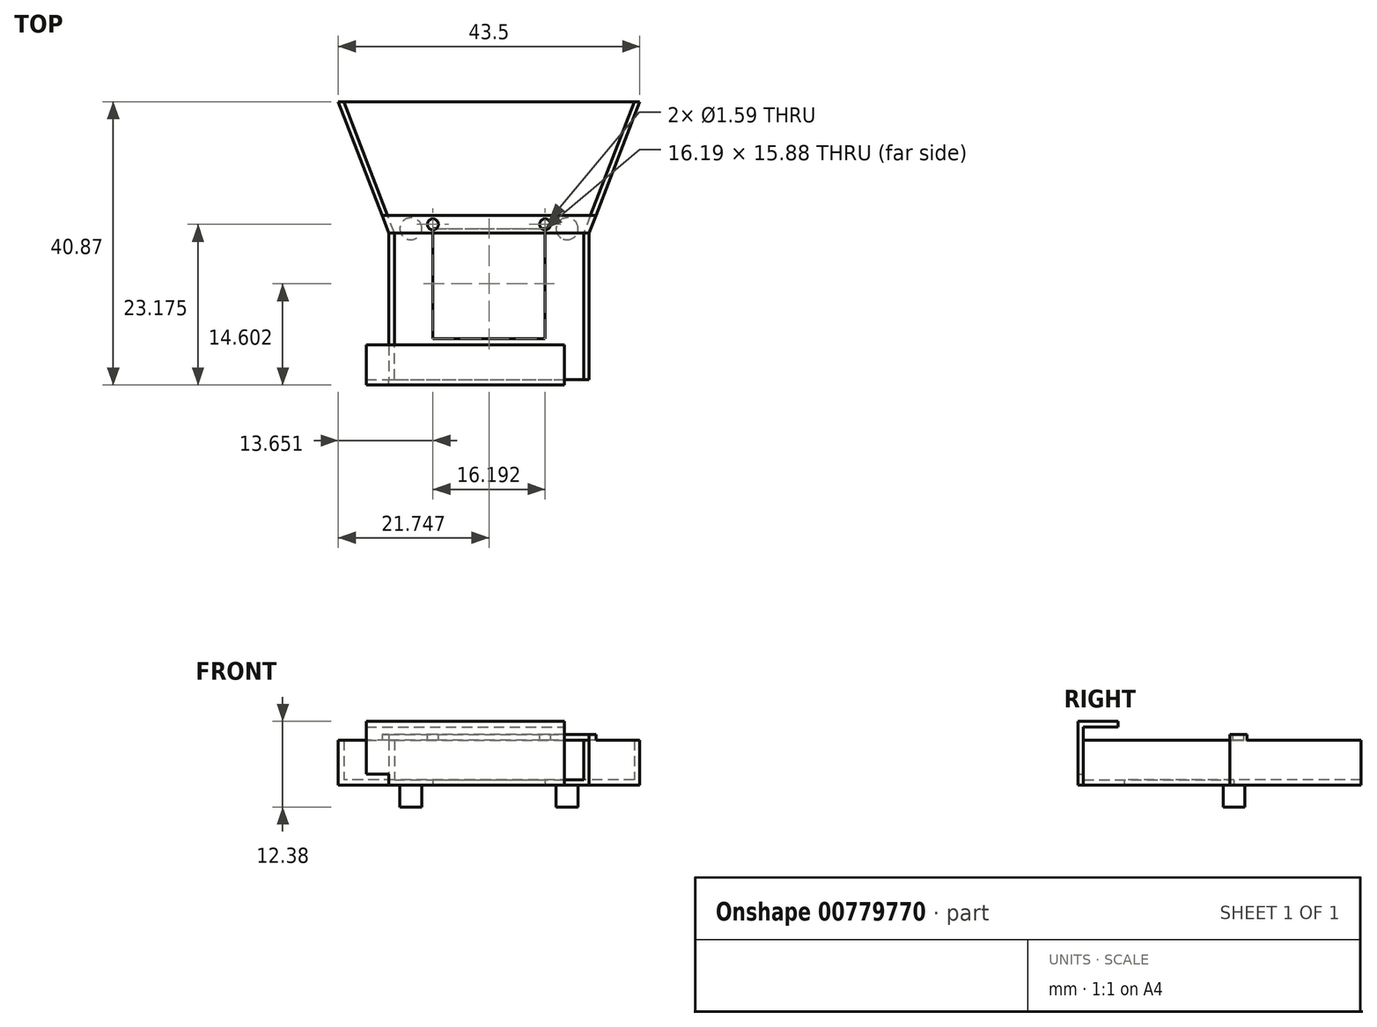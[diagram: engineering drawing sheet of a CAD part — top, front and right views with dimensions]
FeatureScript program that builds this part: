
annotation { "Feature Type Name" : "Feature", "Feature Type Description" : "" }
export const myFeature = defineFeature(function(context is Context, id is Id, definition is map)
    precondition{}
    {
        {
            var Q0;
            Q0=qCreatedBy(makeId("Top.planeOp"),FACE);
            var sketch = newSketch(context, id + "F0", { "sketchPlane" : qUnion([Q0])});
            skLineSegment(sketch, "E0", {"start": v(-18.37, 27.4) * mm, "end": v(-18.37, 7.09) * mm});
            skLineSegment(sketch, "E1", {"start": v(-18.37, 7.09) * mm, "end": v(10.52, 7.09) * mm});
            skLineSegment(sketch, "E2", {"start": v(10.52, 7.09) * mm, "end": v(10.52, 27.4) * mm});
            skLineSegment(sketch, "E3", {"start": v(10.52, 27.4) * mm, "end": v(17.83, 46.37) * mm});
            skLineSegment(sketch, "E4", {"start": v(17.83, 46.37) * mm, "end": v(-25.67, 46.37) * mm});
            skLineSegment(sketch, "E5", {"start": v(-25.67, 46.37) * mm, "end": v(-18.37, 27.4) * mm});
            skLineSegment(sketch, "E6.bottom", {"start": v(-12.02, 28.04) * mm, "end": v(4.17, 28.04) * mm});
            skLineSegment(sketch, "E6.top", {"start": v(-12.02, 12.17) * mm, "end": v(4.17, 12.17) * mm});
            skLineSegment(sketch, "E6.left", {"start": v(-12.02, 28.04) * mm, "end": v(-12.02, 12.17) * mm});
            skLineSegment(sketch, "E6.right", {"start": v(4.17, 28.04) * mm, "end": v(4.17, 12.17) * mm});
            skSolve(sketch);
        }
        {
            var Q0;
            Q0=makeQuery(id+"F0.imprint","IMPRINT",FACE,{"disambiguationData":[TD([[makeQuery(id+"F0.imprint","IMPRINT",EDGE,{"derivedFrom":sQuery(id+"F0.wireOp",EDGE,"E0")}),1.0]])]});
            extrude(context, id + "F1", {"entities" : qUnion([Q0]), "depth" : 0.32 * mm, "offsetDistance" : 25.4 * mm});
        }
        {
            var Q0;
            Q0=makeQuery(id+"F1.opExtrude","CAP_FACE",FACE,{"disambiguationData":[OSD([sQuery(id+"F0.wireOp",EDGE,"E0"),sQuery(id+"F0.wireOp",EDGE,"E1"),sQuery(id+"F0.wireOp",EDGE,"E2"),sQuery(id+"F0.wireOp",EDGE,"E3"),sQuery(id+"F0.wireOp",EDGE,"E4"),sQuery(id+"F0.wireOp",EDGE,"E5"),sQuery(id+"F0.wireOp",EDGE,"E6.bottom"),sQuery(id+"F0.wireOp",EDGE,"E6.top"),sQuery(id+"F0.wireOp",EDGE,"E6.left"),sQuery(id+"F0.wireOp",EDGE,"E6.right")])],"isStart":false});
            var sketch = newSketch(context, id + "F2", { "sketchPlane" : qUnion([Q0])});
            skLineSegment(sketch, "E7", {"start": v(-25.67, 46.37) * mm, "end": v(-18.37, 27.4) * mm});
            skLineSegment(sketch, "E8", {"start": v(-18.37, 27.4) * mm, "end": v(-18.37, 7.09) * mm});
            skLineSegment(sketch, "E9", {"start": v(-18.37, 7.09) * mm, "end": v(-17.58, 7.09) * mm});
            skLineSegment(sketch, "E10", {"start": v(-17.58, 7.09) * mm, "end": v(-17.58, 27.4) * mm});
            skLineSegment(sketch, "E11", {"start": v(-17.58, 27.4) * mm, "end": v(-24.88, 46.37) * mm});
            skLineSegment(sketch, "E12", {"start": v(-24.88, 46.37) * mm, "end": v(-25.67, 46.37) * mm});
            skLineSegment(sketch, "E13", {"start": v(10.52, 7.09) * mm, "end": v(10.52, 27.4) * mm});
            skLineSegment(sketch, "E14", {"start": v(10.52, 27.4) * mm, "end": v(17.83, 46.37) * mm});
            skLineSegment(sketch, "E15", {"start": v(17.83, 46.37) * mm, "end": v(17.03, 46.37) * mm});
            skLineSegment(sketch, "E16", {"start": v(17.03, 46.37) * mm, "end": v(9.73, 27.4) * mm});
            skLineSegment(sketch, "E17", {"start": v(9.73, 27.4) * mm, "end": v(9.73, 7.09) * mm});
            skLineSegment(sketch, "E18", {"start": v(9.73, 7.09) * mm, "end": v(10.52, 7.09) * mm});
            skSolve(sketch);
        }
        {
            var Q0;
            Q0=makeQuery(id+"F2.imprint","IMPRINT",FACE,{"disambiguationData":[TD([[makeQuery(id+"F2.imprint","IMPRINT",EDGE,{"derivedFrom":sQuery(id+"F2.wireOp",EDGE,"E13")}),1.0]])]});
            var Q1;
            Q1=makeQuery(id+"F2.imprint","IMPRINT",FACE,{"disambiguationData":[TD([[makeQuery(id+"F2.imprint","IMPRINT",EDGE,{"derivedFrom":sQuery(id+"F2.wireOp",EDGE,"E7")}),1.0]])]});
            extrude(context, id + "F3", {"entities" : qUnion([Q0, Q1]), "operationType" : NewBodyOperationType.ADD, "depth" : 5.7 * mm, "offsetDistance" : 25.4 * mm});
        }
        {
            var Q0;
            Q0=makeQuery(id+"F3.opExtrude","CAP_FACE",FACE,{"disambiguationData":[OSD([sQuery(id+"F2.wireOp",EDGE,"E7"),sQuery(id+"F2.wireOp",EDGE,"E8"),sQuery(id+"F2.wireOp",EDGE,"E9"),sQuery(id+"F2.wireOp",EDGE,"E10"),sQuery(id+"F2.wireOp",EDGE,"E11"),sQuery(id+"F2.wireOp",EDGE,"E12")])],"isStart":false});
            var sketch = newSketch(context, id + "F4", { "sketchPlane" : qUnion([Q0])});
            skLineSegment(sketch, "E19", {"start": v(-18.37, 27.4) * mm, "end": v(10.52, 27.4) * mm});
            skLineSegment(sketch, "E20", {"start": v(10.52, 27.4) * mm, "end": v(11.5, 29.95) * mm});
            skLineSegment(sketch, "E21", {"start": v(11.5, 29.95) * mm, "end": v(-19.35, 29.95) * mm});
            skLineSegment(sketch, "E22", {"start": v(-19.35, 29.95) * mm, "end": v(-18.37, 27.4) * mm});
            skSolve(sketch);
        }
        {
            var Q0;
            Q0 = qSketchRegion(id + "F4", true);
            extrude(context, id + "F5", {"entities" : qUnion([Q0]), "operationType" : NewBodyOperationType.ADD, "depth" : 0.8 * mm, "offsetDistance" : 25.4 * mm});
        }
        {
            var Q0;
            Q0=makeQuery(id+"F5.opExtrude","CAP_FACE",FACE,{"disambiguationData":[OSD([sQuery(id+"F4.wireOp",EDGE,"E19"),sQuery(id+"F4.wireOp",EDGE,"E20"),sQuery(id+"F4.wireOp",EDGE,"E21"),sQuery(id+"F4.wireOp",EDGE,"E22")])],"isStart":false});
            var sketch = newSketch(context, id + "F6", { "sketchPlane" : qUnion([Q0])});
            skCircle(sketch, "E23", {"center": v(-12.02, 28.68) * mm, "radius": 0.8 * mm});
            skCircle(sketch, "E24", {"center": v(4.17, 28.68) * mm, "radius": 0.8 * mm});
            skSolve(sketch);
        }
        {
            var Q0;
            Q0=makeQuery(id+"F6.imprint","IMPRINT",FACE,{"disambiguationData":[TD([[makeQuery(id+"F6.imprint","IMPRINT",EDGE,{"derivedFrom":sQuery(id+"F6.wireOp",EDGE,"E23")}),1.0]])]});
            var Q1;
            Q1=makeQuery(id+"F6.imprint","IMPRINT",FACE,{"disambiguationData":[TD([[makeQuery(id+"F6.imprint","IMPRINT",EDGE,{"derivedFrom":sQuery(id+"F6.wireOp",EDGE,"E24")}),1.0]])]});
            extrude(context, id + "F7", {"entities" : qUnion([Q0, Q1]), "operationType" : NewBodyOperationType.REMOVE, "oppositeDirection" : true, "depth" : 0.8 * mm, "offsetDistance" : 25.4 * mm});
        }
        {
            var Q0;
            Q0=makeQuery(id+"F1.opExtrude","CAP_FACE",FACE,{"disambiguationData":[OSD([sQuery(id+"F0.wireOp",EDGE,"E0"),sQuery(id+"F0.wireOp",EDGE,"E1"),sQuery(id+"F0.wireOp",EDGE,"E2"),sQuery(id+"F0.wireOp",EDGE,"E3"),sQuery(id+"F0.wireOp",EDGE,"E4"),sQuery(id+"F0.wireOp",EDGE,"E5"),sQuery(id+"F0.wireOp",EDGE,"E6.bottom"),sQuery(id+"F0.wireOp",EDGE,"E6.top"),sQuery(id+"F0.wireOp",EDGE,"E6.left"),sQuery(id+"F0.wireOp",EDGE,"E6.right")])],"isStart":true});
            extrude(context, id + "F8", {"entities" : qUnion([Q0]), "operationType" : NewBodyOperationType.ADD, "depth" : 0.32 * mm, "offsetDistance" : 25.4 * mm});
        }
        {
            var Q0;
            {var subQ0=sQuery(id+"F0.wireOp",EDGE,"E1");Q0=makeQuery(id+"F8.boolean.opBoolean","MERGE",FACE,{"derivedFrom":[makeQuery(id+"F3.boolean.opBoolean","MERGE",FACE,{"derivedFrom":[makeQuery(id+"F1.opExtrude","SWEPT_FACE",FACE,{"disambiguationData":[OSD([subQ0])]}),makeQuery(id+"F3.opExtrude","SWEPT_FACE",FACE,{"disambiguationData":[OSD([sQuery(id+"F2.wireOp",EDGE,"E9")])]}),makeQuery(id+"F3.opExtrude","SWEPT_FACE",FACE,{"disambiguationData":[OSD([sQuery(id+"F2.wireOp",EDGE,"E18")])]})]}),makeQuery(id+"F8.opExtrude","SWEPT_FACE",FACE,{"disambiguationData":[OSD([subQ0])]})]});}
            var sketch = newSketch(context, id + "F9", { "sketchPlane" : qUnion([Q0])});
            skLineSegment(sketch, "E25.bottom", {"start": v(-18.37, 0.32) * mm, "end": v(-16.78, 0.32) * mm});
            skLineSegment(sketch, "E25.top", {"start": v(-18.37, -0.32) * mm, "end": v(-16.78, -0.32) * mm});
            skLineSegment(sketch, "E25.left", {"start": v(-18.37, 0.32) * mm, "end": v(-18.37, -0.32) * mm});
            skLineSegment(sketch, "E25.right", {"start": v(-16.78, 0.32) * mm, "end": v(-16.78, -0.32) * mm});
            skLineSegment(sketch, "E26.bottom", {"start": v(-15.2, 0.32) * mm, "end": v(-13.6, 0.32) * mm});
            skLineSegment(sketch, "E26.top", {"start": v(-15.2, -0.32) * mm, "end": v(-13.6, -0.32) * mm});
            skLineSegment(sketch, "E26.left", {"start": v(-15.2, 0.32) * mm, "end": v(-15.2, -0.32) * mm});
            skLineSegment(sketch, "E26.right", {"start": v(-13.6, 0.32) * mm, "end": v(-13.6, -0.32) * mm});
            skLineSegment(sketch, "E27.bottom", {"start": v(5.35, 0.32) * mm, "end": v(3.76, 0.32) * mm});
            skLineSegment(sketch, "E27.top", {"start": v(5.35, -0.32) * mm, "end": v(3.76, -0.32) * mm});
            skLineSegment(sketch, "E27.left", {"start": v(5.35, 0.32) * mm, "end": v(5.35, -0.32) * mm});
            skLineSegment(sketch, "E27.right", {"start": v(3.76, 0.32) * mm, "end": v(3.76, -0.32) * mm});
            skLineSegment(sketch, "E28.bottom", {"start": v(2.17, 0.32) * mm, "end": v(0.59, 0.32) * mm});
            skLineSegment(sketch, "E28.top", {"start": v(2.17, -0.32) * mm, "end": v(0.59, -0.32) * mm});
            skLineSegment(sketch, "E28.left", {"start": v(2.17, 0.32) * mm, "end": v(2.17, -0.32) * mm});
            skLineSegment(sketch, "E28.right", {"start": v(0.59, 0.32) * mm, "end": v(0.59, -0.32) * mm});
            skSolve(sketch);
        }
        {
            var Q0;
            Q0=makeQuery(id+"F9.imprint","IMPRINT",FACE,{"disambiguationData":[TD([[makeQuery(id+"F9.imprint","IMPRINT",EDGE,{"derivedFrom":sQuery(id+"F9.wireOp",EDGE,"E25.bottom")}),-1.0]])]});
            var Q1;
            Q1=makeQuery(id+"F9.imprint","IMPRINT",FACE,{"disambiguationData":[TD([[makeQuery(id+"F9.imprint","IMPRINT",EDGE,{"derivedFrom":sQuery(id+"F9.wireOp",EDGE,"E26.bottom")}),-1.0]])]});
            var Q2;
            Q2=makeQuery(id+"F9.imprint","IMPRINT",FACE,{"disambiguationData":[TD([[makeQuery(id+"F9.imprint","IMPRINT",EDGE,{"derivedFrom":sQuery(id+"F9.wireOp",EDGE,"E28.bottom")}),-1.0]])]});
            var Q3;
            Q3=makeQuery(id+"F9.imprint","IMPRINT",FACE,{"disambiguationData":[TD([[makeQuery(id+"F9.imprint","IMPRINT",EDGE,{"derivedFrom":sQuery(id+"F9.wireOp",EDGE,"E27.bottom")}),-1.0]])]});
            extrude(context, id + "F10", {"entities" : qUnion([Q0, Q1, Q2, Q3]), "operationType" : NewBodyOperationType.ADD, "depth" : 1.59 * mm, "offsetDistance" : 25.4 * mm});
        }
        {
            var Q0;
            Q0=makeQuery(id+"F10.boolean.opBoolean","MERGE",FACE,{"derivedFrom":[makeQuery(id+"F8.opExtrude","CAP_FACE",FACE,{"disambiguationData":[OSD([sQuery(id+"F0.wireOp",EDGE,"E0"),sQuery(id+"F0.wireOp",EDGE,"E1"),sQuery(id+"F0.wireOp",EDGE,"E2"),sQuery(id+"F0.wireOp",EDGE,"E3"),sQuery(id+"F0.wireOp",EDGE,"E4"),sQuery(id+"F0.wireOp",EDGE,"E5"),sQuery(id+"F0.wireOp",EDGE,"E6.bottom"),sQuery(id+"F0.wireOp",EDGE,"E6.top"),sQuery(id+"F0.wireOp",EDGE,"E6.left"),sQuery(id+"F0.wireOp",EDGE,"E6.right")])],"isStart":false}),makeQuery(id+"F10.opExtrude","SWEPT_FACE",FACE,{"disambiguationData":[OSD([sQuery(id+"F9.wireOp",EDGE,"E25.top")])]}),makeQuery(id+"F10.opExtrude","SWEPT_FACE",FACE,{"disambiguationData":[OSD([sQuery(id+"F9.wireOp",EDGE,"E26.top")])]}),makeQuery(id+"F10.opExtrude","SWEPT_FACE",FACE,{"disambiguationData":[OSD([sQuery(id+"F9.wireOp",EDGE,"E27.top")])]}),makeQuery(id+"F10.opExtrude","SWEPT_FACE",FACE,{"disambiguationData":[OSD([sQuery(id+"F9.wireOp",EDGE,"E28.top")])]})]});
            extrude(context, id + "F11", {"entities" : qUnion([Q0]), "operationType" : NewBodyOperationType.ADD, "depth" : 0.32 * mm, "offsetDistance" : 25.4 * mm});
        }
        {
            var Q0;
            Q0=makeQuery(id+"F10.boolean.opBoolean","MERGE",FACE,{"derivedFrom":[makeQuery(id+"F1.opExtrude","CAP_FACE",FACE,{"disambiguationData":[OSD([sQuery(id+"F0.wireOp",EDGE,"E0"),sQuery(id+"F0.wireOp",EDGE,"E1"),sQuery(id+"F0.wireOp",EDGE,"E2"),sQuery(id+"F0.wireOp",EDGE,"E3"),sQuery(id+"F0.wireOp",EDGE,"E4"),sQuery(id+"F0.wireOp",EDGE,"E5"),sQuery(id+"F0.wireOp",EDGE,"E6.bottom"),sQuery(id+"F0.wireOp",EDGE,"E6.top"),sQuery(id+"F0.wireOp",EDGE,"E6.left"),sQuery(id+"F0.wireOp",EDGE,"E6.right")])],"isStart":false}),makeQuery(id+"F10.opExtrude","SWEPT_FACE",FACE,{"disambiguationData":[OSD([sQuery(id+"F9.wireOp",EDGE,"E25.bottom")])]}),makeQuery(id+"F10.opExtrude","SWEPT_FACE",FACE,{"disambiguationData":[OSD([sQuery(id+"F9.wireOp",EDGE,"E26.bottom")])]}),makeQuery(id+"F10.opExtrude","SWEPT_FACE",FACE,{"disambiguationData":[OSD([sQuery(id+"F9.wireOp",EDGE,"E27.bottom")])]}),makeQuery(id+"F10.opExtrude","SWEPT_FACE",FACE,{"disambiguationData":[OSD([sQuery(id+"F9.wireOp",EDGE,"E28.bottom")])]})]});
            var sketch = newSketch(context, id + "F12", { "sketchPlane" : qUnion([Q0])});
            skLineSegment(sketch, "E29.bottom", {"start": v(-16.78, 7.09) * mm, "end": v(-18.37, 7.09) * mm});
            skLineSegment(sketch, "E29.top", {"start": v(-16.78, 5.5) * mm, "end": v(-18.37, 5.5) * mm});
            skLineSegment(sketch, "E29.left", {"start": v(-16.78, 7.09) * mm, "end": v(-16.78, 5.5) * mm});
            skLineSegment(sketch, "E29.right", {"start": v(-18.37, 7.09) * mm, "end": v(-18.37, 5.5) * mm});
            skLineSegment(sketch, "E30.bottom", {"start": v(-15.2, 7.09) * mm, "end": v(-13.6, 7.09) * mm});
            skLineSegment(sketch, "E30.top", {"start": v(-15.2, 5.5) * mm, "end": v(-13.6, 5.5) * mm});
            skLineSegment(sketch, "E30.left", {"start": v(-15.2, 7.09) * mm, "end": v(-15.2, 5.5) * mm});
            skLineSegment(sketch, "E30.right", {"start": v(-13.6, 7.09) * mm, "end": v(-13.6, 5.5) * mm});
            skLineSegment(sketch, "E31.bottom", {"start": v(0.59, 7.09) * mm, "end": v(2.17, 7.09) * mm});
            skLineSegment(sketch, "E31.top", {"start": v(0.59, 5.5) * mm, "end": v(2.17, 5.5) * mm});
            skLineSegment(sketch, "E31.left", {"start": v(0.59, 7.09) * mm, "end": v(0.59, 5.5) * mm});
            skLineSegment(sketch, "E31.right", {"start": v(2.17, 7.09) * mm, "end": v(2.17, 5.5) * mm});
            skLineSegment(sketch, "E32.bottom", {"start": v(3.76, 7.09) * mm, "end": v(5.35, 7.09) * mm});
            skLineSegment(sketch, "E32.top", {"start": v(3.76, 5.5) * mm, "end": v(5.35, 5.5) * mm});
            skLineSegment(sketch, "E32.left", {"start": v(3.76, 7.09) * mm, "end": v(3.76, 5.5) * mm});
            skLineSegment(sketch, "E32.right", {"start": v(5.35, 7.09) * mm, "end": v(5.35, 5.5) * mm});
            skSolve(sketch);
        }
        {
            var Q0;
            Q0 = qSketchRegion(id + "F12", true);
            extrude(context, id + "F13", {"entities" : qUnion([Q0]), "operationType" : NewBodyOperationType.ADD, "depth" : 0.8 * mm, "offsetDistance" : 25.4 * mm});
        }
        {
            var Q0;
            Q0=makeQuery(id+"F11.opExtrude","CAP_FACE",FACE,{"disambiguationData":[OSD([sQuery(id+"F0.wireOp",EDGE,"E0"),sQuery(id+"F0.wireOp",EDGE,"E1"),sQuery(id+"F0.wireOp",EDGE,"E2"),sQuery(id+"F0.wireOp",EDGE,"E3"),sQuery(id+"F0.wireOp",EDGE,"E4"),sQuery(id+"F0.wireOp",EDGE,"E5"),sQuery(id+"F0.wireOp",EDGE,"E6.bottom"),sQuery(id+"F0.wireOp",EDGE,"E6.top"),sQuery(id+"F0.wireOp",EDGE,"E6.left"),sQuery(id+"F0.wireOp",EDGE,"E6.right"),sQuery(id+"F9.wireOp",EDGE,"E25.top"),sQuery(id+"F9.wireOp",EDGE,"E26.top"),sQuery(id+"F9.wireOp",EDGE,"E27.top"),sQuery(id+"F9.wireOp",EDGE,"E28.top")])],"isStart":false});
            extrude(context, id + "F14", {"entities" : qUnion([Q0]), "operationType" : NewBodyOperationType.REMOVE, "oppositeDirection" : true, "depth" : 0.16 * mm, "offsetDistance" : 25.4 * mm});
        }
        {
            var Q0;
            {var subQ0=sQuery(id+"F9.wireOp",EDGE,"E25.left");var subQ1=sQuery(id+"F0.wireOp",EDGE,"E0");Q0=makeQuery(id+"F13.boolean.opBoolean","MERGE",FACE,{"derivedFrom":[makeQuery(id+"F11.boolean.opBoolean","MERGE",FACE,{"derivedFrom":[makeQuery(id+"F10.boolean.opBoolean","MERGE",FACE,{"derivedFrom":[makeQuery(id+"F8.boolean.opBoolean","MERGE",FACE,{"derivedFrom":[makeQuery(id+"F3.boolean.opBoolean","MERGE",FACE,{"derivedFrom":[makeQuery(id+"F1.opExtrude","SWEPT_FACE",FACE,{"disambiguationData":[OSD([subQ1])]}),makeQuery(id+"F3.opExtrude","SWEPT_FACE",FACE,{"disambiguationData":[OSD([sQuery(id+"F2.wireOp",EDGE,"E8")])]})]}),makeQuery(id+"F8.opExtrude","SWEPT_FACE",FACE,{"disambiguationData":[OSD([subQ1])]})]}),makeQuery(id+"F10.opExtrude","SWEPT_FACE",FACE,{"disambiguationData":[OSD([subQ0])]})]}),makeQuery(id+"F11.opExtrude","SWEPT_FACE",FACE,{"disambiguationData":[OSD([subQ1,sQuery(id+"F9.wireOp",EDGE,"E25.top"),subQ0])]})]}),makeQuery(id+"F13.opExtrude","SWEPT_FACE",FACE,{"disambiguationData":[OSD([sQuery(id+"F12.wireOp",EDGE,"E29.right")])]})]});}
            var sketch = newSketch(context, id + "F15", { "sketchPlane" : qUnion([Q0])});
            skCircle(sketch, "E33", {"center": v(-6.3, 0.32) * mm, "radius": 0.5 * mm});
            skPoint(sketch, "E33.centerSnap0", {"position": v(-5.5, 0.32) * mm});
            skPoint(sketch, "E33.centerSnap1", {"position": v(-6.3, 1.11) * mm});
            skSolve(sketch);
        }
        {
            var Q0;
            Q0=makeQuery(id+"F15.imprint","IMPRINT",FACE,{"disambiguationData":[TD([[makeQuery(id+"F15.imprint","IMPRINT",EDGE,{"derivedFrom":sQuery(id+"F15.wireOp",EDGE,"E33")}),1.0]])]});
            extrude(context, id + "F16", {"entities" : qUnion([Q0]), "operationType" : NewBodyOperationType.REMOVE, "oppositeDirection" : true, "depth" : 25.4 * mm, "offsetDistance" : 25.4 * mm});
        }
        {
            var Q0;
            Q0=makeQuery(id+"F14.boolean.opBoolean","COPY",FACE,{"derivedFrom":makeQuery(id+"F14.opExtrude","CAP_FACE",FACE,{"disambiguationData":[OSD([sQuery(id+"F0.wireOp",EDGE,"E0"),sQuery(id+"F0.wireOp",EDGE,"E1"),sQuery(id+"F0.wireOp",EDGE,"E2"),sQuery(id+"F0.wireOp",EDGE,"E3"),sQuery(id+"F0.wireOp",EDGE,"E4"),sQuery(id+"F0.wireOp",EDGE,"E5"),sQuery(id+"F0.wireOp",EDGE,"E6.bottom"),sQuery(id+"F0.wireOp",EDGE,"E6.top"),sQuery(id+"F0.wireOp",EDGE,"E6.left"),sQuery(id+"F0.wireOp",EDGE,"E6.right"),sQuery(id+"F9.wireOp",EDGE,"E25.top"),sQuery(id+"F9.wireOp",EDGE,"E26.top"),sQuery(id+"F9.wireOp",EDGE,"E27.top"),sQuery(id+"F9.wireOp",EDGE,"E28.top")])],"isStart":false})});
            var sketch = newSketch(context, id + "F17", { "sketchPlane" : qUnion([Q0])});
            skCircle(sketch, "E34", {"center": v(-15.2, -28.04) * mm, "radius": 1.59 * mm});
            skCircle(sketch, "E35", {"center": v(7.35, -28.04) * mm, "radius": 1.59 * mm});
            skSolve(sketch);
        }
        {
            var Q0;
            Q0=makeQuery(id+"F17.imprint","IMPRINT",FACE,{"disambiguationData":[TD([[makeQuery(id+"F17.imprint","IMPRINT",EDGE,{"derivedFrom":sQuery(id+"F17.wireOp",EDGE,"E34")}),1.0]])]});
            var Q1;
            Q1=makeQuery(id+"F17.imprint","IMPRINT",FACE,{"disambiguationData":[TD([[makeQuery(id+"F17.imprint","IMPRINT",EDGE,{"derivedFrom":sQuery(id+"F17.wireOp",EDGE,"E35")}),1.0]])]});
            extrude(context, id + "F18", {"entities" : qUnion([Q0, Q1]), "operationType" : NewBodyOperationType.ADD, "depth" : 3.17 * mm, "offsetDistance" : 25.4 * mm});
        }
        {
            var Q0;
            {var subQ0=sQuery(id+"F9.wireOp",EDGE,"E27.left");Q0=makeQuery(id+"F13.boolean.opBoolean","MERGE",FACE,{"derivedFrom":[makeQuery(id+"F11.boolean.opBoolean","MERGE",FACE,{"derivedFrom":[makeQuery(id+"F10.opExtrude","SWEPT_FACE",FACE,{"disambiguationData":[OSD([subQ0])]}),makeQuery(id+"F11.opExtrude","SWEPT_FACE",FACE,{"disambiguationData":[OSD([sQuery(id+"F0.wireOp",EDGE,"E1"),sQuery(id+"F9.wireOp",EDGE,"E27.top"),subQ0])]})]}),makeQuery(id+"F13.opExtrude","SWEPT_FACE",FACE,{"disambiguationData":[OSD([sQuery(id+"F12.wireOp",EDGE,"E32.right")])]})]});}
            var Q1;
            {var subQ0=sQuery(id+"F9.wireOp",EDGE,"E28.left");Q1=makeQuery(id+"F13.boolean.opBoolean","MERGE",FACE,{"derivedFrom":[makeQuery(id+"F11.boolean.opBoolean","MERGE",FACE,{"derivedFrom":[makeQuery(id+"F10.opExtrude","SWEPT_FACE",FACE,{"disambiguationData":[OSD([subQ0])]}),makeQuery(id+"F11.opExtrude","SWEPT_FACE",FACE,{"disambiguationData":[OSD([sQuery(id+"F0.wireOp",EDGE,"E1"),sQuery(id+"F9.wireOp",EDGE,"E28.top"),subQ0])]})]}),makeQuery(id+"F13.opExtrude","SWEPT_FACE",FACE,{"disambiguationData":[OSD([sQuery(id+"F12.wireOp",EDGE,"E31.right")])]})]});}
            var Q2;
            {var subQ0=sQuery(id+"F9.wireOp",EDGE,"E25.right");Q2=makeQuery(id+"F13.boolean.opBoolean","MERGE",FACE,{"derivedFrom":[makeQuery(id+"F11.boolean.opBoolean","MERGE",FACE,{"derivedFrom":[makeQuery(id+"F10.opExtrude","SWEPT_FACE",FACE,{"disambiguationData":[OSD([subQ0])]}),makeQuery(id+"F11.opExtrude","SWEPT_FACE",FACE,{"disambiguationData":[OSD([sQuery(id+"F0.wireOp",EDGE,"E1"),sQuery(id+"F9.wireOp",EDGE,"E25.top"),subQ0])]})]}),makeQuery(id+"F13.opExtrude","SWEPT_FACE",FACE,{"disambiguationData":[OSD([sQuery(id+"F12.wireOp",EDGE,"E29.left")])]})]});}
            var Q3;
            {var subQ0=sQuery(id+"F9.wireOp",EDGE,"E26.right");Q3=makeQuery(id+"F13.boolean.opBoolean","MERGE",FACE,{"derivedFrom":[makeQuery(id+"F11.boolean.opBoolean","MERGE",FACE,{"derivedFrom":[makeQuery(id+"F10.opExtrude","SWEPT_FACE",FACE,{"disambiguationData":[OSD([subQ0])]}),makeQuery(id+"F11.opExtrude","SWEPT_FACE",FACE,{"disambiguationData":[OSD([sQuery(id+"F0.wireOp",EDGE,"E1"),sQuery(id+"F9.wireOp",EDGE,"E26.top"),subQ0])]})]}),makeQuery(id+"F13.opExtrude","SWEPT_FACE",FACE,{"disambiguationData":[OSD([sQuery(id+"F12.wireOp",EDGE,"E30.right")])]})]});}
            extrude(context, id + "F19", {"entities" : qUnion([Q0, Q1, Q2, Q3]), "operationType" : NewBodyOperationType.ADD, "depth" : 1.59 * mm, "offsetDistance" : 25.4 * mm});
        }
        {
            var Q0;
            Q0=makeQuery(id+"F19.opExtrude","CAP_FACE",FACE,{"disambiguationData":[OSD([sQuery(id+"F0.wireOp",EDGE,"E1"),sQuery(id+"F9.wireOp",EDGE,"E26.top"),sQuery(id+"F9.wireOp",EDGE,"E26.right"),sQuery(id+"F12.wireOp",EDGE,"E30.right")])],"isStart":false});
            extrude(context, id + "F20", {"entities" : qUnion([Q0]), "operationType" : NewBodyOperationType.ADD, "depth" : 12.7 * mm, "offsetDistance" : 25.4 * mm});
        }
        {
            var Q0;
            Q0=makeQuery(id+"F19.opExtrude","CAP_FACE",FACE,{"disambiguationData":[OSD([sQuery(id+"F0.wireOp",EDGE,"E1"),sQuery(id+"F9.wireOp",EDGE,"E27.top"),sQuery(id+"F9.wireOp",EDGE,"E27.left"),sQuery(id+"F12.wireOp",EDGE,"E32.right")])],"isStart":false});
            var sketch = newSketch(context, id + "F21", { "sketchPlane" : qUnion([Q0])});
            skCircle(sketch, "E36", {"center": v(6.3, 0.32) * mm, "radius": 0.5 * mm});
            skSolve(sketch);
        }
        {
            var Q0;
            Q0=makeQuery(id+"F21.imprint","IMPRINT",FACE,{"disambiguationData":[TD([[makeQuery(id+"F21.imprint","IMPRINT",EDGE,{"derivedFrom":sQuery(id+"F21.wireOp",EDGE,"E36")}),1.0]])]});
            extrude(context, id + "F22", {"entities" : qUnion([Q0]), "operationType" : NewBodyOperationType.ADD, "oppositeDirection" : true, "depth" : 25.3 * mm, "offsetDistance" : 25.4 * mm});
        }
        {
            var Q0;
            {var subQ0=sQuery(id+"F9.wireOp",EDGE,"E25.left");var subQ1=sQuery(id+"F0.wireOp",EDGE,"E0");Q0=makeQuery(id+"F22.boolean.opBoolean","MERGE",FACE,{"derivedFrom":[makeQuery(id+"F13.boolean.opBoolean","MERGE",FACE,{"derivedFrom":[makeQuery(id+"F11.boolean.opBoolean","MERGE",FACE,{"derivedFrom":[makeQuery(id+"F10.boolean.opBoolean","MERGE",FACE,{"derivedFrom":[makeQuery(id+"F8.boolean.opBoolean","MERGE",FACE,{"derivedFrom":[makeQuery(id+"F3.boolean.opBoolean","MERGE",FACE,{"derivedFrom":[makeQuery(id+"F1.opExtrude","SWEPT_FACE",FACE,{"disambiguationData":[OSD([subQ1])]}),makeQuery(id+"F3.opExtrude","SWEPT_FACE",FACE,{"disambiguationData":[OSD([sQuery(id+"F2.wireOp",EDGE,"E8")])]})]}),makeQuery(id+"F8.opExtrude","SWEPT_FACE",FACE,{"disambiguationData":[OSD([subQ1])]})]}),makeQuery(id+"F10.opExtrude","SWEPT_FACE",FACE,{"disambiguationData":[OSD([subQ0])]})]}),makeQuery(id+"F11.opExtrude","SWEPT_FACE",FACE,{"disambiguationData":[OSD([subQ1,sQuery(id+"F9.wireOp",EDGE,"E25.top"),subQ0])]})]}),makeQuery(id+"F13.opExtrude","SWEPT_FACE",FACE,{"disambiguationData":[OSD([sQuery(id+"F12.wireOp",EDGE,"E29.right")])]})]}),makeQuery(id+"F22.opExtrude","CAP_FACE",FACE,{"disambiguationData":[OSD([sQuery(id+"F21.wireOp",EDGE,"E36")])],"isStart":false})]});}
            var sketch = newSketch(context, id + "F23", { "sketchPlane" : qUnion([Q0])});
            skLineSegment(sketch, "E37.bottom", {"start": v(-7.09, 1.11) * mm, "end": v(-5.5, 1.11) * mm});
            skLineSegment(sketch, "E37.top", {"start": v(-7.09, -0.48) * mm, "end": v(-5.5, -0.48) * mm});
            skLineSegment(sketch, "E37.left", {"start": v(-7.09, 1.11) * mm, "end": v(-7.09, -0.48) * mm});
            skLineSegment(sketch, "E37.right", {"start": v(-5.5, 1.11) * mm, "end": v(-5.5, -0.48) * mm});
            skSolve(sketch);
        }
        {
            var Q0;
            Q0=makeQuery(id+"F23.imprint","IMPRINT",FACE,{"disambiguationData":[TD([[makeQuery(id+"F23.imprint","IMPRINT",EDGE,{"derivedFrom":sQuery(id+"F23.wireOp",EDGE,"E37.bottom")}),1.0]])]});
            extrude(context, id + "F24", {"entities" : qUnion([Q0]), "operationType" : NewBodyOperationType.ADD, "depth" : 3.27 * mm, "offsetDistance" : 25.4 * mm});
        }
        {
            var Q0;
            {var subQ0=sQuery(id+"F12.wireOp",EDGE,"E30.right");var subQ1=sQuery(id+"F12.wireOp",EDGE,"E32.right");var subQ2=sQuery(id+"F12.wireOp",EDGE,"E31.right");var subQ3=sQuery(id+"F12.wireOp",EDGE,"E29.left");Q0=makeQuery(id+"F24.boolean.opBoolean","MERGE",FACE,{"derivedFrom":[makeQuery(id+"F20.boolean.opBoolean","MERGE",FACE,{"derivedFrom":[makeQuery(id+"F19.boolean.opBoolean","MERGE",FACE,{"derivedFrom":[makeQuery(id+"F13.opExtrude","CAP_FACE",FACE,{"disambiguationData":[OSD([sQuery(id+"F12.wireOp",EDGE,"E29.bottom"),sQuery(id+"F12.wireOp",EDGE,"E29.top"),subQ3,sQuery(id+"F12.wireOp",EDGE,"E29.right")])],"isStart":false}),makeQuery(id+"F13.opExtrude","CAP_FACE",FACE,{"disambiguationData":[OSD([sQuery(id+"F12.wireOp",EDGE,"E30.bottom"),sQuery(id+"F12.wireOp",EDGE,"E30.top"),sQuery(id+"F12.wireOp",EDGE,"E30.left"),subQ0])],"isStart":false}),makeQuery(id+"F19.opExtrude","SWEPT_FACE",FACE,{"disambiguationData":[OSD([subQ3])]}),makeQuery(id+"F19.opExtrude","SWEPT_FACE",FACE,{"disambiguationData":[OSD([subQ0])]})]}),makeQuery(id+"F19.boolean.opBoolean","MERGE",FACE,{"derivedFrom":[makeQuery(id+"F13.opExtrude","CAP_FACE",FACE,{"disambiguationData":[OSD([sQuery(id+"F12.wireOp",EDGE,"E31.bottom"),sQuery(id+"F12.wireOp",EDGE,"E31.top"),sQuery(id+"F12.wireOp",EDGE,"E31.left"),subQ2])],"isStart":false}),makeQuery(id+"F13.opExtrude","CAP_FACE",FACE,{"disambiguationData":[OSD([sQuery(id+"F12.wireOp",EDGE,"E32.bottom"),sQuery(id+"F12.wireOp",EDGE,"E32.top"),sQuery(id+"F12.wireOp",EDGE,"E32.left"),subQ1])],"isStart":false}),makeQuery(id+"F19.opExtrude","SWEPT_FACE",FACE,{"disambiguationData":[OSD([subQ2])]}),makeQuery(id+"F19.opExtrude","SWEPT_FACE",FACE,{"disambiguationData":[OSD([subQ1])]})]}),makeQuery(id+"F20.opExtrude","SWEPT_FACE",FACE,{"disambiguationData":[OSD([subQ0])]})]}),makeQuery(id+"F24.opExtrude","SWEPT_FACE",FACE,{"disambiguationData":[OSD([sQuery(id+"F23.wireOp",EDGE,"E37.bottom")])]})]});}
            var sketch = newSketch(context, id + "F25", { "sketchPlane" : qUnion([Q0])});
            skLineSegment(sketch, "E38.bottom", {"start": v(-21.64, 6.3) * mm, "end": v(6.94, 6.3) * mm});
            skLineSegment(sketch, "E38.top", {"start": v(-21.64, 5.5) * mm, "end": v(6.94, 5.5) * mm});
            skLineSegment(sketch, "E38.left", {"start": v(-21.64, 6.3) * mm, "end": v(-21.64, 5.5) * mm});
            skLineSegment(sketch, "E38.right", {"start": v(6.94, 6.3) * mm, "end": v(6.94, 5.5) * mm});
            skSolve(sketch);
        }
        {
            var Q0;
            Q0=makeQuery(id+"F25.imprint","IMPRINT",FACE,{"disambiguationData":[TD([[makeQuery(id+"F25.imprint","IMPRINT",EDGE,{"derivedFrom":sQuery(id+"F25.wireOp",EDGE,"E38.bottom")}),-1.0]])]});
            extrude(context, id + "F26", {"entities" : qUnion([Q0]), "operationType" : NewBodyOperationType.ADD, "depth" : 7.62 * mm, "offsetDistance" : 25.4 * mm});
        }
        {
            var Q0;
            {var subQ0=sQuery(id+"F12.wireOp",EDGE,"E30.right");var subQ1=sQuery(id+"F12.wireOp",EDGE,"E30.bottom");var subQ2=sQuery(id+"F9.wireOp",EDGE,"E26.right");var subQ3=sQuery(id+"F9.wireOp",EDGE,"E26.top");var subQ4=sQuery(id+"F0.wireOp",EDGE,"E1");var subQ5=sQuery(id+"F12.wireOp",EDGE,"E31.bottom");var subQ6=sQuery(id+"F12.wireOp",EDGE,"E32.bottom");var subQ7=sQuery(id+"F12.wireOp",EDGE,"E29.bottom");Q0=makeQuery(id+"F20.boolean.opBoolean","MERGE",FACE,{"derivedFrom":[makeQuery(id+"F19.boolean.opBoolean","MERGE",FACE,{"derivedFrom":[makeQuery(id+"F13.opExtrude","SWEPT_FACE",FACE,{"disambiguationData":[OSD([subQ1])]}),makeQuery(id+"F13.opExtrude","SWEPT_FACE",FACE,{"disambiguationData":[OSD([subQ7])]}),makeQuery(id+"F19.opExtrude","SWEPT_FACE",FACE,{"disambiguationData":[OSD([subQ4,sQuery(id+"F9.wireOp",EDGE,"E25.top"),sQuery(id+"F9.wireOp",EDGE,"E25.right"),subQ7,sQuery(id+"F12.wireOp",EDGE,"E29.left")])]}),makeQuery(id+"F19.opExtrude","SWEPT_FACE",FACE,{"disambiguationData":[OSD([subQ4,subQ3,subQ2,subQ1,subQ0])]})]}),makeQuery(id+"F19.boolean.opBoolean","MERGE",FACE,{"derivedFrom":[makeQuery(id+"F13.opExtrude","SWEPT_FACE",FACE,{"disambiguationData":[OSD([subQ5])]}),makeQuery(id+"F13.opExtrude","SWEPT_FACE",FACE,{"disambiguationData":[OSD([subQ6])]}),makeQuery(id+"F19.opExtrude","SWEPT_FACE",FACE,{"disambiguationData":[OSD([subQ4,sQuery(id+"F9.wireOp",EDGE,"E27.top"),sQuery(id+"F9.wireOp",EDGE,"E27.left"),subQ6,sQuery(id+"F12.wireOp",EDGE,"E32.right")])]}),makeQuery(id+"F19.opExtrude","SWEPT_FACE",FACE,{"disambiguationData":[OSD([subQ4,sQuery(id+"F9.wireOp",EDGE,"E28.top"),sQuery(id+"F9.wireOp",EDGE,"E28.left"),subQ5,sQuery(id+"F12.wireOp",EDGE,"E31.right")])]})]}),makeQuery(id+"F20.opExtrude","SWEPT_FACE",FACE,{"disambiguationData":[OSD([subQ4,subQ3,subQ2,subQ1,subQ0])]})]});}
            extrude(context, id + "F27", {"entities" : qUnion([Q0]), "operationType" : NewBodyOperationType.REMOVE, "oppositeDirection" : true, "depth" : 0.8 * mm, "offsetDistance" : 25.4 * mm});
        }
        {
            var Q0;
            {var subQ0=sQuery(id+"F0.wireOp",EDGE,"E0");var subQ1=sQuery(id+"F0.wireOp",EDGE,"E1");var subQ3=sQuery(id+"F2.wireOp",EDGE,"E9");Q0=makeQuery(id+"F10.boolean.opBoolean","SPLIT",FACE,{"disambiguationData":[TD([makeQuery(id+"F1.opExtrude","SWEPT_FACE",FACE,{"disambiguationData":[OSD([subQ0])]})])],"derivedFrom":makeQuery(id+"F8.boolean.opBoolean","MERGE",FACE,{"derivedFrom":[makeQuery(id+"F3.boolean.opBoolean","MERGE",FACE,{"derivedFrom":[makeQuery(id+"F1.opExtrude","SWEPT_FACE",FACE,{"disambiguationData":[OSD([subQ1])]}),makeQuery(id+"F3.opExtrude","SWEPT_FACE",FACE,{"disambiguationData":[OSD([subQ3])]}),makeQuery(id+"F3.opExtrude","SWEPT_FACE",FACE,{"disambiguationData":[OSD([sQuery(id+"F2.wireOp",EDGE,"E18")])]})]}),makeQuery(id+"F8.opExtrude","SWEPT_FACE",FACE,{"disambiguationData":[OSD([subQ1])]})]})});}
            extrude(context, id + "F28", {"entities" : qUnion([Q0]), "operationType" : NewBodyOperationType.ADD, "depth" : 0.8 * mm, "offsetDistance" : 25.4 * mm});
        }
        {
            var Q0;
            {var subQ8=sQuery(id+"F0.wireOp",EDGE,"E2");var subQ9=sQuery(id+"F0.wireOp",EDGE,"E1");var subQ14=makeQuery(id+"F1.opExtrude","SWEPT_FACE",FACE,{"disambiguationData":[OSD([subQ8])]});var subQ15=makeQuery(id+"F1.opExtrude","SWEPT_FACE",FACE,{"disambiguationData":[OSD([subQ9])]});var subQ16=makeQuery(id+"F8.opExtrude","SWEPT_FACE",FACE,{"disambiguationData":[OSD([subQ9])]});var subQ18=sQuery(id+"F2.wireOp",EDGE,"E18");var subQ19=makeQuery(id+"F3.opExtrude","SWEPT_FACE",FACE,{"disambiguationData":[OSD([subQ18])]});var subQ20=makeQuery(id+"F3.opExtrude","SWEPT_FACE",FACE,{"disambiguationData":[OSD([sQuery(id+"F2.wireOp",EDGE,"E9")])]});Q0=makeQuery(id+"F11.boolean.opBoolean","MERGE",FACE,{"derivedFrom":[makeQuery(id+"F10.boolean.opBoolean","SPLIT",FACE,{"disambiguationData":[TD([subQ14])],"derivedFrom":makeQuery(id+"F8.boolean.opBoolean","MERGE",FACE,{"derivedFrom":[makeQuery(id+"F3.boolean.opBoolean","MERGE",FACE,{"derivedFrom":[subQ15,subQ20,subQ19]}),subQ16]})}),makeQuery(id+"F11.opExtrude","SWEPT_FACE",FACE,{"disambiguationData":[OSD([subQ9]),TDD([makeQuery(id+"F10.boolean.opBoolean","SPLIT",EDGE,{"disambiguationData":[TD([subQ14])],"derivedFrom":makeQuery(id+"F8.opExtrude","CAP_EDGE",EDGE,{"disambiguationData":[OSD([subQ9])],"isStart":false})})])]})]});}
            extrude(context, id + "F29", {"entities" : qUnion([Q0]), "operationType" : NewBodyOperationType.ADD, "depth" : 0.8 * mm, "offsetDistance" : 25.4 * mm});
        }
        {
            var Q0;
            Q0=makeQuery(id+"F24.opExtrude","SWEPT_FACE",FACE,{"disambiguationData":[OSD([sQuery(id+"F23.wireOp",EDGE,"E37.left")])]});
            extrude(context, id + "F30", {"entities" : qUnion([Q0]), "operationType" : NewBodyOperationType.REMOVE, "oppositeDirection" : true, "depth" : 25.4 * mm, "offsetDistance" : 25.4 * mm});
        }
        {
            var Q0;
            Q0=makeQuery(id+"F27.boolean.opBoolean","MERGE",FACE,{"derivedFrom":[makeQuery(id+"F26.opExtrude","SWEPT_FACE",FACE,{"disambiguationData":[OSD([sQuery(id+"F25.wireOp",EDGE,"E38.bottom")])]})],"fromTools":[makeQuery(id+"F27.opExtrude","CAP_FACE",FACE,{"disambiguationData":[OSD([sQuery(id+"F0.wireOp",EDGE,"E1"),sQuery(id+"F9.wireOp",EDGE,"E25.top"),sQuery(id+"F9.wireOp",EDGE,"E25.right"),sQuery(id+"F9.wireOp",EDGE,"E26.top"),sQuery(id+"F9.wireOp",EDGE,"E26.right"),sQuery(id+"F9.wireOp",EDGE,"E27.top"),sQuery(id+"F9.wireOp",EDGE,"E27.left"),sQuery(id+"F9.wireOp",EDGE,"E28.top"),sQuery(id+"F9.wireOp",EDGE,"E28.left"),sQuery(id+"F12.wireOp",EDGE,"E29.bottom"),sQuery(id+"F12.wireOp",EDGE,"E29.left"),sQuery(id+"F12.wireOp",EDGE,"E30.bottom"),sQuery(id+"F12.wireOp",EDGE,"E30.right"),sQuery(id+"F12.wireOp",EDGE,"E31.bottom"),sQuery(id+"F12.wireOp",EDGE,"E31.right"),sQuery(id+"F12.wireOp",EDGE,"E32.bottom"),sQuery(id+"F12.wireOp",EDGE,"E32.right")])],"isStart":false})]});
            var sketch = newSketch(context, id + "F31", { "sketchPlane" : qUnion([Q0])});
            skLineSegment(sketch, "E39.bottom", {"start": v(21.64, 7.94) * mm, "end": v(-6.94, 7.94) * mm});
            skLineSegment(sketch, "E39.top", {"start": v(21.64, 8.73) * mm, "end": v(-6.94, 8.73) * mm});
            skLineSegment(sketch, "E39.left", {"start": v(21.64, 7.94) * mm, "end": v(21.64, 8.73) * mm});
            skLineSegment(sketch, "E39.right", {"start": v(-6.94, 7.94) * mm, "end": v(-6.94, 8.73) * mm});
            skSolve(sketch);
        }
        {
            var Q0;
            Q0=makeQuery(id+"F31.imprint","IMPRINT",FACE,{"disambiguationData":[TD([[makeQuery(id+"F31.imprint","IMPRINT",EDGE,{"derivedFrom":sQuery(id+"F31.wireOp",EDGE,"E39.bottom")}),-1.0]])]});
            extrude(context, id + "F32", {"entities" : qUnion([Q0]), "operationType" : NewBodyOperationType.ADD, "depth" : 5 * mm, "offsetDistance" : 25.4 * mm});
        }
    });
